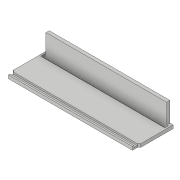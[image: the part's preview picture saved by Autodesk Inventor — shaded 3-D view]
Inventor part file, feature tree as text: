
AUTODESK INVENTOR PART (.ipt)
format: ipt  version: 2018.3 (Build 223284000, 284)  size: 139,776 bytes
history: native  units: in
note: dims shown in document units (in); Inventor stores cm internally (conversion verified against a paired STEP export)
features: extrude x5, sketch x5, fillet x1
ambient origin geometry x8: Origin, YZ Plane, XZ Plane, XY Plane, X Axis, Y Axis, Z Axis, Center Point
bodies: Solid1 (feature_tree)
feature tree (11):
  extrude  "Extrusion1"  Depth=1.5in
  extrude  "Extrusion2"  Depth=0.126in
  extrude  "Extrusion3"  Depth=0.0625in
  extrude  "Extrusion4"  Depth=0.135in
  fillet  "Fillet1"  Radius=0.125in
  extrude  "Extrusion5"  Depth=0.135in
  sketch  "Sketch1"  dims[d0=4.875in d1=1.5in]
  sketch  "Sketch2"  dims[d2=0.125in d3=0.0in d4=0.126in]
  sketch  "Sketch3"  dims[d5=0.0625in d8=3.375in]
  sketch  "Sketch4"  dims[d9=0.0625in d10=0.135in d11=0.125in]
  sketch  "Sketch5"  dims[d12=0.0625in d13=0.0in d15=0.135in d16=0.125in d17=0.0625in d18=0.5in d19=0.0in d20=0.0625in d21=0.0625in d22=0.25in d23=0.25in d24=0.0625in d25=0.5in d26=0.0in d27=0.0625in d29=0.75in d30=0.0in d31=0.125in d32=0.126in d33=0.126in]
